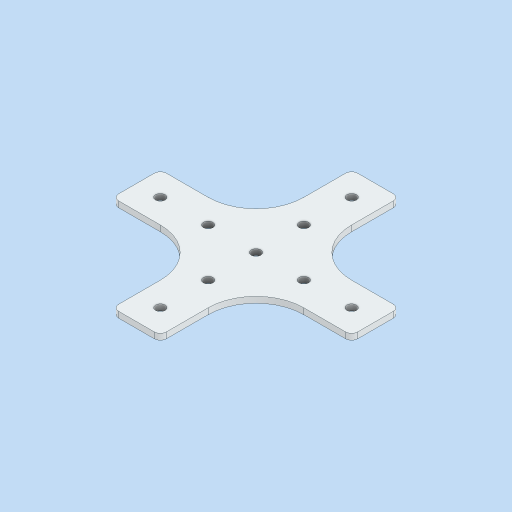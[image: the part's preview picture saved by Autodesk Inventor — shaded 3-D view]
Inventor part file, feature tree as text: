
AUTODESK INVENTOR PART (.ipt)
format: ipt  version: 2024 (Build 280153000, 153)  size: 136,704 bytes
history: native  units: in
note: dims shown in document units (in); Inventor stores cm internally (conversion verified against a paired STEP export)
features: fillet x1
ambient origin geometry x8: Origin, YZ Plane, XZ Plane, XY Plane, X Axis, Y Axis, Z Axis, Center Point
bodies: Solid1 (feature_tree)
feature tree (1):
  fillet  "Fillet2"  [1 undecoded]
note: 1 required parameter value undecoded (feature->parameter linkage not recoverable at this tier; creation-order binding heuristic only, values carry confidence <= 0.55)
